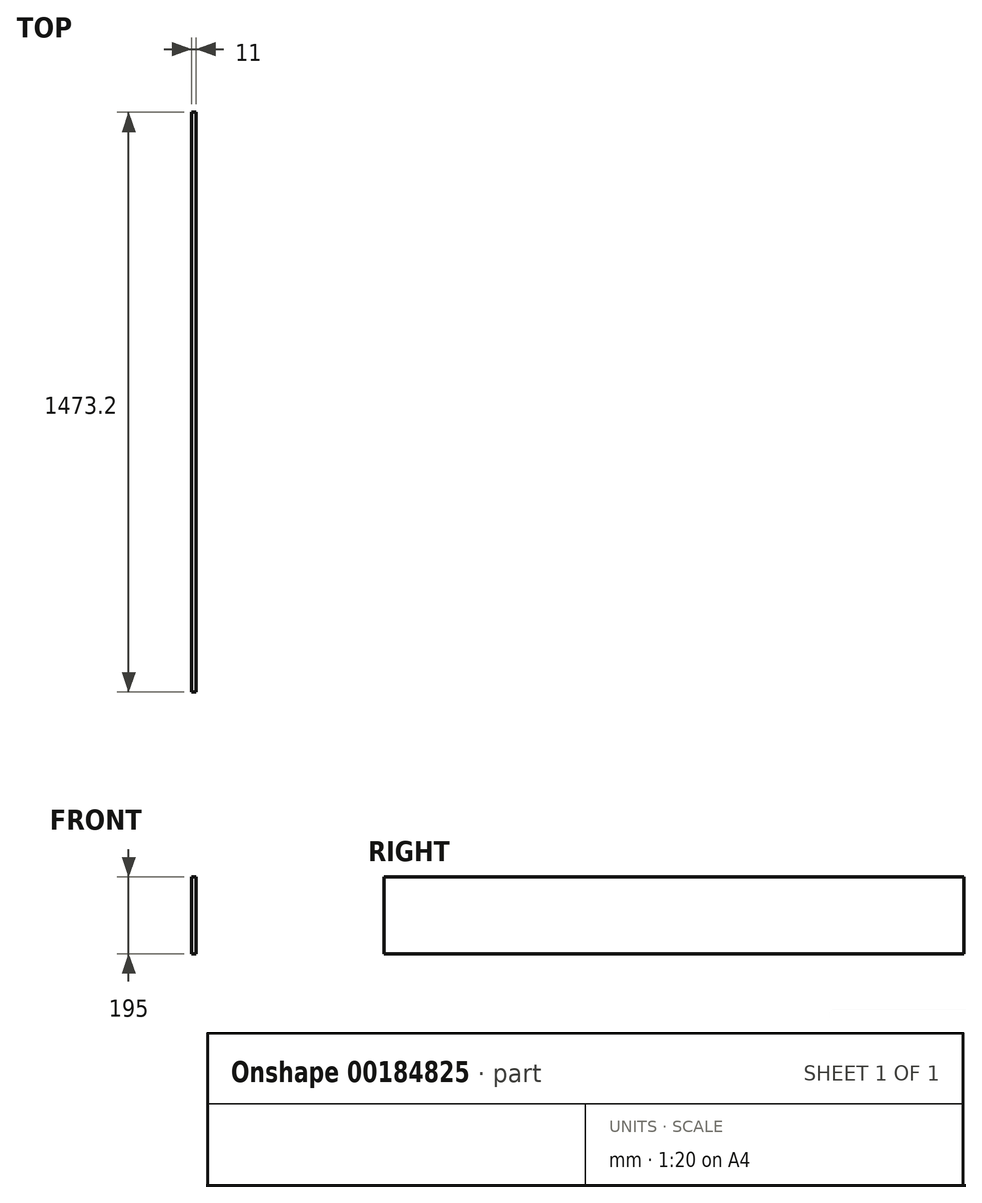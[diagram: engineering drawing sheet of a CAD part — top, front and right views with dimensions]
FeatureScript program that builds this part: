
annotation { "Feature Type Name" : "Feature", "Feature Type Description" : "" }
export const myFeature = defineFeature(function(context is Context, id is Id, definition is map)
    precondition{}
    {
        {
            var Q0;
            Q0=qCreatedBy(makeId("Front.planeOp"),FACE);
            var sketch = newSketch(context, id + "F0", { "sketchPlane" : qUnion([Q0])});
            skLineSegment(sketch, "E0.bottom", {"start": v(0, 0) * mm, "end": v(11, 0) * mm});
            skLineSegment(sketch, "E0.top", {"start": v(0, 195) * mm, "end": v(11, 195) * mm});
            skLineSegment(sketch, "E0.left", {"start": v(0, 0) * mm, "end": v(0, 195) * mm});
            skLineSegment(sketch, "E0.right", {"start": v(11, 0) * mm, "end": v(11, 195) * mm});
            skSolve(sketch);
        }
        {
            var Q0;
            Q0=makeQuery(id+"F0.imprint","IMPRINT",FACE,{"disambiguationData":[TD([[makeQuery(id+"F0.imprint","IMPRINT",EDGE,{"derivedFrom":sQuery(id+"F0.wireOp",EDGE,"E0.bottom")}),1.0]])]});
            extrude(context, id + "F1", {"entities" : qUnion([Q0]), "depth" : 1473.2 * mm});
        }
    });
